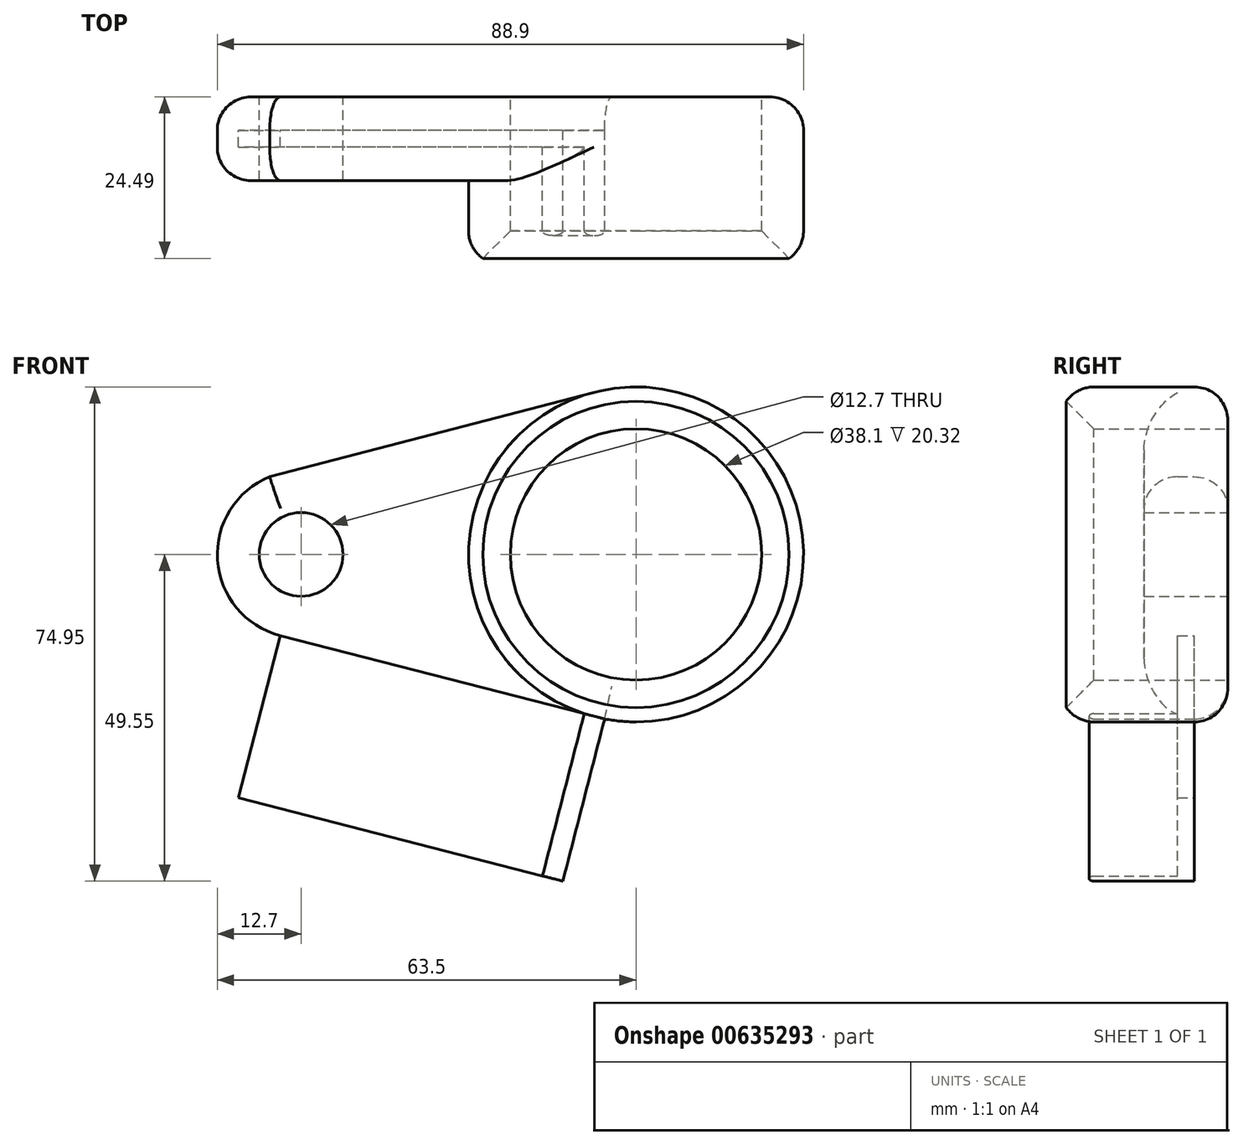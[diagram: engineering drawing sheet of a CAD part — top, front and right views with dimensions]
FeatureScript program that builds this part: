
annotation { "Feature Type Name" : "Feature", "Feature Type Description" : "" }
export const myFeature = defineFeature(function(context is Context, id is Id, definition is map)
    precondition{}
    {
        {
            var Q0;
            Q0=qCreatedBy(makeId("Front.planeOp"),FACE);
            var sketch = newSketch(context, id + "F0", { "sketchPlane" : qUnion([Q0])});
            skCircle(sketch, "E0", {"center": v(0, 0) * mm, "radius": 12.7 * mm});
            skCircle(sketch, "E1", {"center": v(50.8, 0) * mm, "radius": 25.4 * mm});
            skLineSegment(sketch, "E2", {"start": v(-4.76, 11.77) * mm, "end": v(44.4, 24.58) * mm});
            skLineSegment(sketch, "E3", {"start": v(46.04, -24.95) * mm, "end": v(-3.16, -12.3) * mm});
            skCircle(sketch, "E4", {"center": v(50.8, 0) * mm, "radius": 19.05 * mm});
            skCircle(sketch, "E5", {"center": v(0, 0) * mm, "radius": 6.35 * mm});
            skSolve(sketch);
        }
        {
            var Q0;
            {var subQ0=sQuery(id+"F0.wireOp",EDGE,"E2");var subQ1=sQuery(id+"F0.wireOp",EDGE,"E0");var subQ2=makeQuery(id+"F0.imprint","INTERSECT",VERTEX,{"disambiguationData":[OD(0.0)],"derivedFrom":[subQ1,subQ0]});Q0=makeQuery(id+"F0.imprint","IMPRINT",FACE,{"disambiguationData":[TD([[makeQuery(id+"F0.imprint","IMPRINT",EDGE,{"disambiguationData":[TD([[subQ2,1.0]])],"derivedFrom":subQ1}),1.0]])]});}
            var Q1;
            {var subQ0=sQuery(id+"F0.wireOp",EDGE,"E3");var subQ1=sQuery(id+"F0.wireOp",EDGE,"E1");var subQ2=makeQuery(id+"F0.imprint","INTERSECT",VERTEX,{"disambiguationData":[OD(0.0)],"derivedFrom":[subQ1,subQ0]});Q1=makeQuery(id+"F0.imprint","IMPRINT",FACE,{"disambiguationData":[TD([[makeQuery(id+"F0.imprint","IMPRINT",EDGE,{"disambiguationData":[TD([[subQ2,1.0]])],"derivedFrom":subQ1}),1.0]])]});}
            var Q2;
            Q2=makeQuery(id+"F0.imprint","IMPRINT",FACE,{"disambiguationData":[TD([[makeQuery(id+"F0.imprint","IMPRINT",EDGE,{"derivedFrom":sQuery(id+"F0.wireOp",EDGE,"E5")}),-1.0]])]});
            var Q3;
            Q3=makeQuery(id+"F0.imprint","IMPRINT",FACE,{"disambiguationData":[TD([[makeQuery(id+"F0.imprint","IMPRINT",EDGE,{"derivedFrom":sQuery(id+"F0.wireOp",EDGE,"E4")}),-1.0]])]});
            var Q4;
            {var subQ0=sQuery(id+"F0.wireOp",EDGE,"E3");var subQ1=sQuery(id+"F0.wireOp",EDGE,"E0");var subQ2=makeQuery(id+"F0.imprint","INTERSECT",VERTEX,{"derivedFrom":[subQ1,subQ0]});Q4=makeQuery(id+"F0.imprint","IMPRINT",FACE,{"disambiguationData":[TD([[makeQuery(id+"F0.imprint","IMPRINT",EDGE,{"disambiguationData":[TD([[subQ2,-1.0]])],"derivedFrom":subQ1}),-1.0]])]});}
            extrude(context, id + "F1", {"entities" : qUnion([Q0, Q1, Q2, Q3, Q4]), "depth" : 12.7 * mm, "offsetDistance" : 25.4 * mm});
        }
        {
            var Q0;
            Q0=makeQuery(id+"F0.imprint","IMPRINT",FACE,{"disambiguationData":[TD([[makeQuery(id+"F0.imprint","IMPRINT",EDGE,{"derivedFrom":sQuery(id+"F0.wireOp",EDGE,"E4")}),-1.0]])]});
            extrude(context, id + "F2", {"entities" : qUnion([Q0]), "operationType" : NewBodyOperationType.ADD, "depth" : 25.4 * mm, "offsetDistance" : 25.4 * mm});
        }
        {
            var Q0;
            Q0=makeQuery(id+"F1.opExtrude","CAP_EDGE",EDGE,{"disambiguationData":[OSD([sQuery(id+"F0.wireOp",EDGE,"E3")])],"isStart":false});
            var Q1;
            Q1=makeQuery(id+"F1.opExtrude","CAP_EDGE",EDGE,{"disambiguationData":[OSD([sQuery(id+"F0.wireOp",EDGE,"E0")])],"isStart":false});
            var Q2;
            Q2=makeQuery(id+"F1.opExtrude","CAP_EDGE",EDGE,{"disambiguationData":[OSD([sQuery(id+"F0.wireOp",EDGE,"E2")])],"isStart":false});
            fillet(context, id + "F3", {"entities" : qUnion([Q0, Q1, Q2]), "radius" : 5.08 * mm, "tangentPropagation" : true, "allowEdgeOverflow" : false});
        }
        {
            var Q0;
            Q0=makeQuery(id+"F1.opExtrude","CAP_EDGE",EDGE,{"disambiguationData":[OSD([sQuery(id+"F0.wireOp",EDGE,"E2")])],"isStart":true});
            var Q1;
            Q1=makeQuery(id+"F1.opExtrude","CAP_EDGE",EDGE,{"disambiguationData":[OSD([sQuery(id+"F0.wireOp",EDGE,"E0")])],"isStart":true});
            var Q2;
            Q2=makeQuery(id+"F2.opExtrude","CAP_EDGE",EDGE,{"disambiguationData":[OSD([sQuery(id+"F0.wireOp",EDGE,"E1")])],"isStart":false});
            fillet(context, id + "F4", {"entities" : qUnion([Q0, Q1, Q2]), "radius" : 5.08 * mm, "tangentPropagation" : true, "allowEdgeOverflow" : false});
        }
        {
            var Q0;
            Q0=makeQuery(id+"F2.opExtrude","CAP_EDGE",EDGE,{"disambiguationData":[OSD([sQuery(id+"F0.wireOp",EDGE,"E4")])],"isStart":false});
            chamfer(context, id + "F5", {"entities" : qUnion([Q0]), "width" : 5.08 * mm, "tangentPropagation" : true});
        }
        {
            var Q0;
            Q0=makeQuery(id+"F2.opExtrude","SWEPT_FACE",FACE,{"disambiguationData":[OSD([sQuery(id+"F0.wireOp",EDGE,"E3")])]});
            extrude(context, id + "F6", {"entities" : qUnion([Q0]), "operationType" : NewBodyOperationType.ADD, "depth" : 25.4 * mm, "offsetDistance" : 25.4 * mm});
        }
    });
